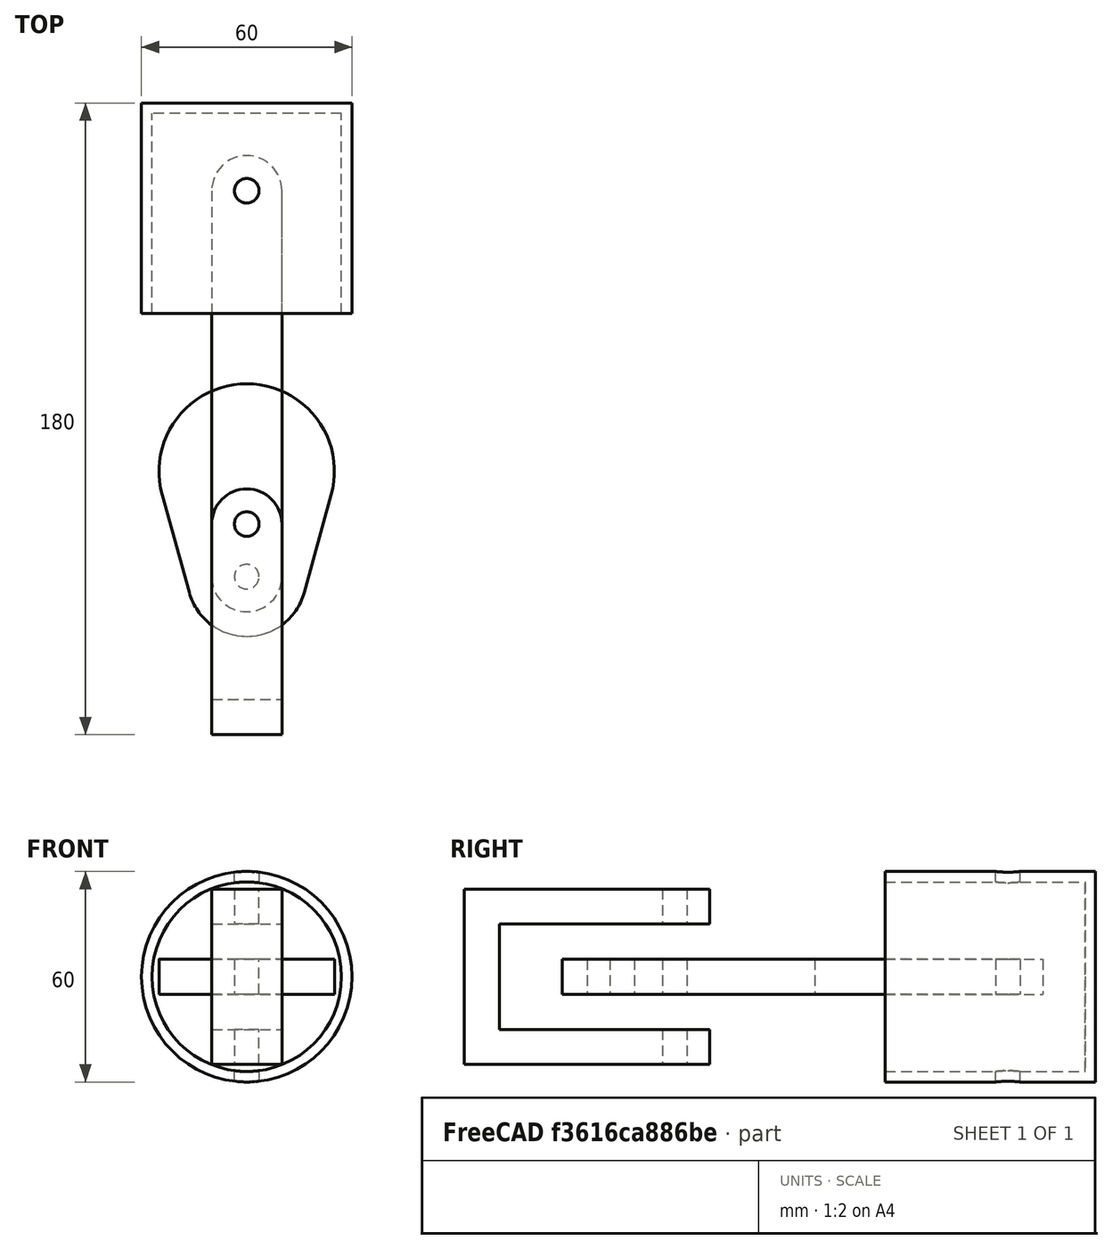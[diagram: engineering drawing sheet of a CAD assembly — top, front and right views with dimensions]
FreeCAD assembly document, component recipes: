
FREECAD ASSEMBLY — COMPONENT RECIPES ("Piston_Head_Assembly")

This assembly document has 5 components, labeled P0..P4 below (a component is one placed body or linked part). 5 of them carry a construction recipe — the FreeCAD feature program that regenerates the part from scratch, quoted from this document or its linked companion documents; the rest are supplied as boundary geometry only. No exploded tour is included for this assembly.
COMPONENT P0 — recipe-attached ("Crank001", modeled in this document).
Construction recipe (the document's own serialized feature program — sketch geometry with constraints, then the solid features built on it; lengths are millimeters unless a unit is written):

FEATURE [PartDesign::SubShapeBinder] Binder002
  BindCopyOnChange = 0
  BindMode = 0
  ClaimChildren = false
  Context = -> Body002 [Binder002.]
  Fuse = false
  MakeFace = false
  OffsetFill = false
  OffsetIntersection = false
  OffsetJoinType = 0
  OffsetOpenResult = false
  PartialLoad = false
  Refine = true
  Relative = true
  Support = -> [Sketch]
  _Version = 2
FEATURE [Sketcher::SketchObject] Sketch004
  ArcFitTolerance = 1e-06
  AttachmentSupport = -> [XY_Plane002]
  ExternalGeometry = -> [Binder002]
  FullyConstrained = true
  MakeInternals = false
  MapMode = 5
  sketch-geometry (6):
    g0: ArcOfCircle CenterX=0 CenterY=-25 CenterZ=0 NormalX=0 NormalY=0 NormalZ=1 AngleXU=0 Radius=25 StartAngle=6.01325 EndAngle=9.69471
    g1: ArcOfCircle CenterX=0 CenterY=-55 CenterZ=0 NormalX=0 NormalY=0 NormalZ=1 AngleXU=0 Radius=17 StartAngle=3.41153 EndAngle=6.01325
    g2: LineSegment StartX=-24.0947 StartY=-31.6667 StartZ=0 EndX=-16.3844 EndY=-59.5333 EndZ=0
    g3: LineSegment StartX=24.0947 StartY=-31.6667 StartZ=0 EndX=16.3844 EndY=-59.5333 EndZ=0
    g4: Circle CenterX=0 CenterY=-40 CenterZ=0 NormalX=0 NormalY=0 NormalZ=1 AngleXU=0 Radius=3.5
    g5: Circle CenterX=0 CenterY=-55 CenterZ=0 NormalX=0 NormalY=0 NormalZ=1 AngleXU=0 Radius=3.5
  constraints (14):
    c: Coincident(g0,g-3)
    c: Coincident(g0,g-5)
    c: Coincident(g1,g-6)
    c: Coincident(g1,g-6)
    c: Horizontal(g1,g1)
    c: Horizontal(g0,g0)
    c: Coincident(g2,g0)
    c: Coincident(g2,g1)
    c: Coincident(g3,g0)
    c: Coincident(g3,g1)
    c: Coincident(g4,g-7)
    c: Coincident(g5,g1)
    c: Equal(g4,g-7)
    c: Equal(g5,g-8)
FEATURE [PartDesign::Pad] Pad001
  Direction = (0,0,1)
  Length = 10
  Length2 = 10
  Midplane = true
  Profile = -> Sketch004
  ReferenceAxis = -> Sketch004 [N_Axis]
  Refine = true
  Suppressed = false
  Type = 0
FEATURE [PartDesign::Body] Body002  label="Crank"
  AllowCompound = false
  Group = -> [Binder002,Sketch004,Pad001]
  Origin = -> Origin002
  Tip = -> Pad001
COMPONENT P1 — same part as P0; its construction recipe is shown at P0.
COMPONENT P2 — recipe-attached ("Link001", modeled in this document).
Construction recipe (the document's own serialized feature program — sketch geometry with constraints, then the solid features built on it; lengths are millimeters unless a unit is written):

FEATURE [PartDesign::SubShapeBinder] Binder
  BindCopyOnChange = 0
  BindMode = 0
  ClaimChildren = false
  Context = -> Body [Binder.]
  Fuse = false
  MakeFace = false
  OffsetFill = false
  OffsetIntersection = false
  OffsetJoinType = 0
  OffsetOpenResult = false
  PartialLoad = false
  Refine = true
  Relative = true
  Support = -> [Sketch]
  _Version = 2
FEATURE [Sketcher::SketchObject] Sketch001
  ArcFitTolerance = 1e-06
  AttachmentSupport = -> [XY_Plane]
  ExternalGeometry = -> [Binder]
  FullyConstrained = true
  MakeInternals = false
  MapMode = 5
  sketch-geometry (6):
    g0: LineSegment StartX=-10 StartY=55 StartZ=0 EndX=-10 EndY=-55 EndZ=0
    g1: ArcOfCircle CenterX=0 CenterY=-55 CenterZ=0 NormalX=0 NormalY=0 NormalZ=1 AngleXU=0 Radius=10 StartAngle=3.14159 EndAngle=6.28319
    g2: LineSegment StartX=10 StartY=-55 StartZ=0 EndX=10 EndY=55 EndZ=0
    g3: ArcOfCircle CenterX=-7.86e-14 CenterY=55 CenterZ=0 NormalX=0 NormalY=0 NormalZ=1 AngleXU=0 Radius=10 StartAngle=4e-16 EndAngle=3.14159
    g4: Circle CenterX=-7.86e-14 CenterY=55 CenterZ=0 NormalX=0 NormalY=0 NormalZ=1 AngleXU=0 Radius=3.5
    g5: Circle CenterX=0 CenterY=-55 CenterZ=0 NormalX=0 NormalY=0 NormalZ=1 AngleXU=0 Radius=3.5
  constraints (12):
    c: Coincident(g-4,g0)
    c: Coincident(g0,g-5)
    c: Tangent(g0,g1) = -1.5708
    c: Coincident(g1,g-6)
    c: Tangent(g1,g2) = -1.5708
    c: Tangent(g2,g3) = -1.5708
    c: Coincident(g3,g0)
    c: Coincident(g4,g3)
    c: Coincident(g5,g1)
    c: Equal(g5,g-7)
    c: Equal(g-8,g4)
    c: Equal(g3,g-3)
FEATURE [PartDesign::Pad] Pad
  Direction = (0,0,1)
  Length = 10
  Length2 = 10
  Midplane = true
  Profile = -> Sketch001
  ReferenceAxis = -> Sketch001 [N_Axis]
  Refine = true
  Suppressed = false
  Type = 0
FEATURE [PartDesign::Body] Body  label="Link"
  AllowCompound = false
  Group = -> [Binder,Sketch001,Pad]
  Origin = -> Origin
  Tip = -> Pad
COMPONENT P3 — recipe-attached ("Mount001", modeled in this document).
Construction recipe (the document's own serialized feature program — sketch geometry with constraints, then the solid features built on it; lengths are millimeters unless a unit is written):

FEATURE [PartDesign::SubShapeBinder] Binder003
  BindCopyOnChange = 0
  BindMode = 0
  ClaimChildren = false
  Context = -> Body003 [Binder003.]
  Fuse = false
  MakeFace = false
  OffsetFill = false
  OffsetIntersection = false
  OffsetJoinType = 0
  OffsetOpenResult = false
  PartialLoad = false
  Refine = true
  Relative = true
  Support = -> [Sketch]
  _Version = 2
FEATURE [Sketcher::SketchObject] Sketch005
  ArcFitTolerance = 1e-06
  AttachmentSupport = -> [XY_Plane003]
  ExternalGeometry = -> [Binder003]
  FullyConstrained = true
  MakeInternals = false
  MapMode = 5
  sketch-geometry (5):
    g0: LineSegment StartX=-10 StartY=-40 StartZ=0 EndX=-10 EndY=-100 EndZ=0
    g1: LineSegment StartX=-10 StartY=-100 StartZ=0 EndX=10 EndY=-100 EndZ=0
    g2: LineSegment StartX=10 StartY=-100 StartZ=0 EndX=10 EndY=-40 EndZ=0
    g3: ArcOfCircle CenterX=8e-16 CenterY=-40 CenterZ=0 NormalX=0 NormalY=0 NormalZ=1 AngleXU=0 Radius=10 StartAngle=0 EndAngle=3.14159
    g4: Circle CenterX=8e-16 CenterY=-40 CenterZ=0 NormalX=0 NormalY=0 NormalZ=1 AngleXU=0 Radius=3.5
  constraints (12):
    c: Coincident(g0,g1)
    c: Coincident(g1,g-7)
    c: Coincident(g1,g2)
    c: Coincident(g2,g-5)
    c: Tangent(g2,g3) = -1.5708
    c: Coincident(g3,g0)
    c: Equal(g0,g-6)
    c: Horizontal(g2,g0)
    c: Equal(g-7,g1)
    c: Coincident(g4,g3)
    c: Equal(g4,g-4)
    c: Equal(g-3,g3)
FEATURE [PartDesign::Pad] Pad002
  Direction = (0,0,1)
  Length = 50
  Length2 = 10
  Midplane = true
  Profile = -> Sketch005
  ReferenceAxis = -> Sketch005 [N_Axis]
  Refine = true
  Suppressed = false
  Type = 0
FEATURE [PartDesign::SubShapeBinder] Binder004
  BindCopyOnChange = 0
  BindMode = 0
  ClaimChildren = false
  Context = -> Body003 [Binder004.]
  Fuse = false
  MakeFace = false
  OffsetFill = false
  OffsetIntersection = false
  OffsetJoinType = 0
  OffsetOpenResult = false
  PartialLoad = false
  Refine = true
  Relative = true
  Support = -> [Body002]
  _Version = 2
FEATURE [Sketcher::SketchObject] Sketch006
  ArcFitTolerance = 1e-06
  AttachmentSupport = -> [Pad002]
  ExternalGeometry = -> [Pad002]
  FullyConstrained = true
  MakeInternals = false
  MapMode = 5
  Placement = pos=(-10,-3e-16,0) rot=(0.57735,-0.57735,-0.57735;2.0944rad)
  sketch-geometry (4):
    g0: LineSegment StartX=0 StartY=15 StartZ=0 EndX=0 EndY=-15 EndZ=0
    g1: LineSegment StartX=0 StartY=-15 StartZ=0 EndX=90 EndY=-15 EndZ=0
    g2: LineSegment StartX=90 StartY=-15 StartZ=0 EndX=90 EndY=15 EndZ=0
    g3: LineSegment StartX=90 StartY=15 StartZ=0 EndX=0 EndY=15 EndZ=0
  constraints (11):
    c: Coincident(g0,g1)
    c: Coincident(g1,g2)
    c: Coincident(g2,g3)
    c: Coincident(g3,g0)
    c: Vertical(g2)
    c: Horizontal(g1)
    c: Horizontal(g3)
    c: PointOnObject(g0,g-2)
    c: Symmetric(g0,g0,g-1)
    c: DistanceY(g2,g2) = 30
    c: Distance(g-3,g2) = 10
FEATURE [PartDesign::Pocket] Pocket001
  BaseFeature = -> Pad002
  Direction = (1,0,0)
  Length = 5
  Length2 = 5
  Profile = -> Sketch006
  ReferenceAxis = -> Sketch006 [N_Axis]
  Refine = true
  Suppressed = false
  Type = 1
FEATURE [PartDesign::Body] Body003  label="Mount"
  AllowCompound = false
  Group = -> [Binder003,Sketch005,Pad002,Binder004,Sketch006,Pocket001]
  Origin = -> Origin003
  Tip = -> Pocket001
COMPONENT P4 — recipe-attached ("Piston_Head001", modeled in this document).
Construction recipe (the document's own serialized feature program — sketch geometry with constraints, then the solid features built on it; lengths are millimeters unless a unit is written):

FEATURE [PartDesign::SubShapeBinder] Binder001
  BindCopyOnChange = 0
  BindMode = 0
  ClaimChildren = false
  Context = -> Body001 [Binder001.]
  Fuse = false
  MakeFace = false
  OffsetFill = false
  OffsetIntersection = false
  OffsetJoinType = 0
  OffsetOpenResult = false
  PartialLoad = false
  Refine = true
  Relative = true
  Support = -> [Sketch]
  _Version = 2
FEATURE [Sketcher::SketchObject] Sketch002
  ArcFitTolerance = 1e-06
  AttachmentSupport = -> [XY_Plane001]
  ExternalGeometry = -> [Binder001]
  FullyConstrained = true
  MakeInternals = false
  MapMode = 5
  sketch-geometry (6):
    g0: LineSegment StartX=0 StartY=80 StartZ=0 EndX=-30 EndY=80 EndZ=0
    g1: LineSegment StartX=-30 StartY=80 StartZ=0 EndX=-30 EndY=20 EndZ=0
    g2: LineSegment StartX=-30 StartY=20 StartZ=0 EndX=-27 EndY=20 EndZ=0
    g3: LineSegment StartX=-27 StartY=20 StartZ=0 EndX=-27 EndY=77 EndZ=0
    g4: LineSegment StartX=-27 StartY=77 StartZ=0 EndX=0 EndY=77 EndZ=0
    g5: LineSegment StartX=0 StartY=77 StartZ=0 EndX=0 EndY=80 EndZ=0
  constraints (15):
    c: Symmetric(g-3,g-3,g0)
    c: Coincident(g0,g-4)
    c: Coincident(g0,g1)
    c: Coincident(g1,g-4)
    c: Coincident(g1,g2)
    c: PointOnObject(g2,g-5)
    c: Coincident(g2,g3)
    c: Vertical(g3)
    c: Coincident(g3,g4)
    c: PointOnObject(g4,g-2)
    c: Horizontal(g4)
    c: Coincident(g4,g5)
    c: Coincident(g5,g0)
    c: DistanceX(g2,g2) = 3
    c: DistanceY(g5,g5) = 3
FEATURE [PartDesign::Revolution] Revolution
  Angle = 360
  Angle2 = 60
  Axis = (1e-16,1,-1e-16)
  Base = (0,0,0)
  Midplane = true
  Profile = -> Sketch002
  ReferenceAxis = -> Y_Axis001
  Refine = true
  Suppressed = false
  Type = 0
FEATURE [Sketcher::SketchObject] Sketch003
  ArcFitTolerance = 1e-06
  AttachmentSupport = -> [XY_Plane001]
  ExternalGeometry = -> [Binder001]
  FullyConstrained = true
  MakeInternals = false
  MapMode = 5
  sketch-geometry (1):
    g0: Circle CenterX=0 CenterY=55 CenterZ=0 NormalX=0 NormalY=0 NormalZ=1 AngleXU=0 Radius=3.5
  constraints (2):
    c: Coincident(g0,g-3)
    c: Equal(g0,g-3)
FEATURE [PartDesign::Pocket] Pocket
  BaseFeature = -> Revolution
  Direction = (0,0,-1)
  Length = 52
  Length2 = 5
  Midplane = true
  Profile = -> Sketch003
  ReferenceAxis = -> Sketch003 [N_Axis]
  Refine = true
  Suppressed = false
  Type = 1
FEATURE [PartDesign::Body] Body001  label="Piston_Head"
  AllowCompound = false
  Group = -> [Binder001,Sketch002,Revolution,Sketch003,Pocket]
  Origin = -> Origin001
  Tip = -> Pocket
PROVENANCE & LICENSES
A FreeCAD (.FCStd) document from a public repository crawl; recipes are the document's own serialized feature recipes (and, for linked parts, companion documents' recipes).
License: as declared in the source repository (recorded in the dataset sidecar).
